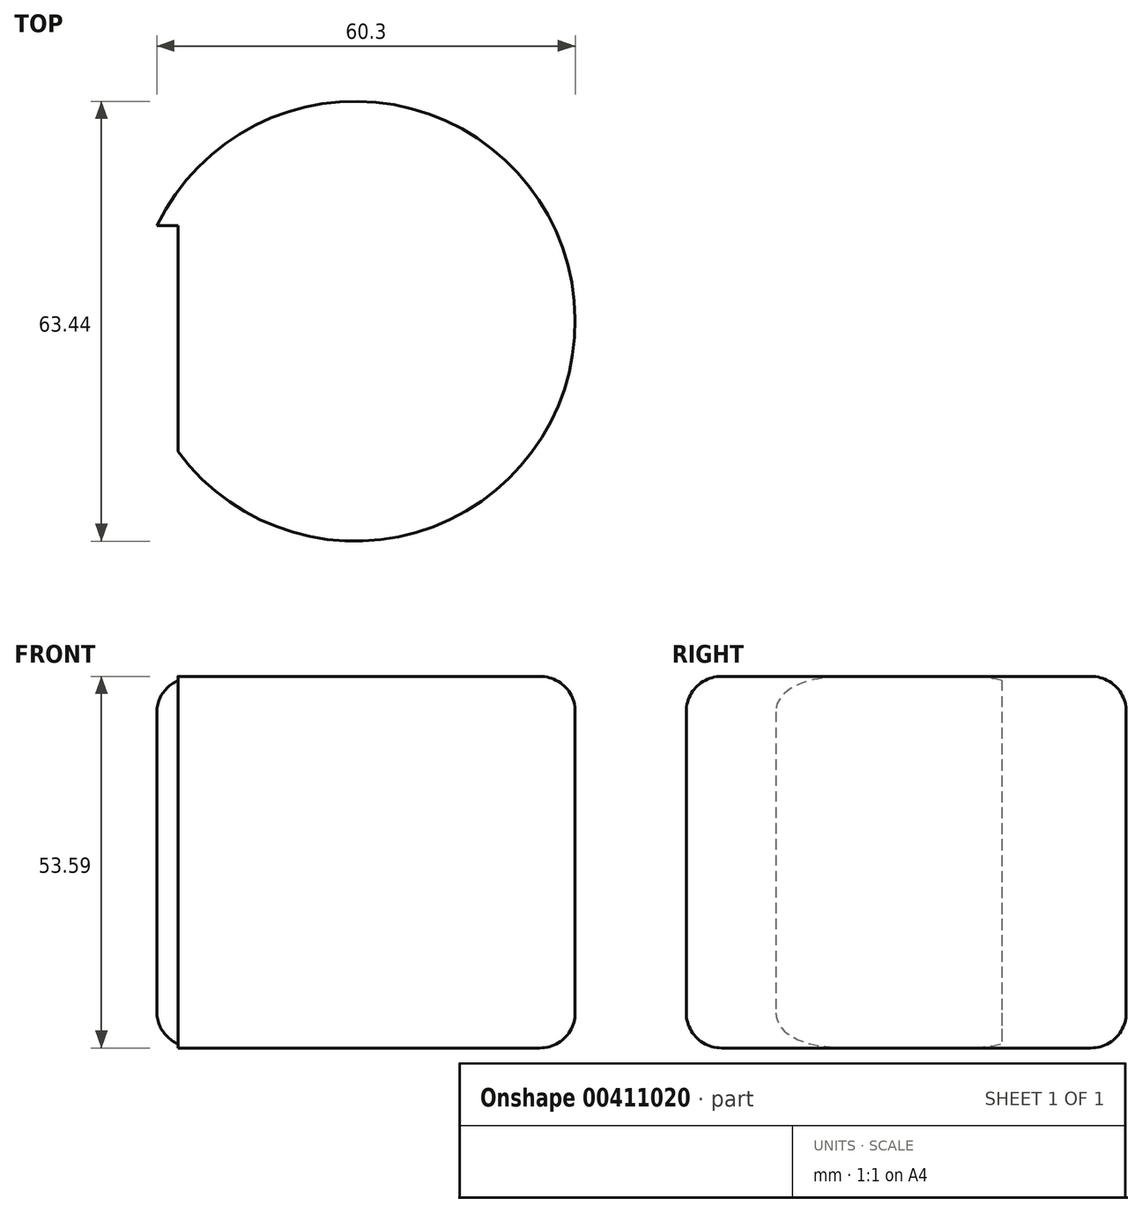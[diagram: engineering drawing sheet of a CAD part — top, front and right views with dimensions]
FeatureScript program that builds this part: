
annotation { "Feature Type Name" : "Feature", "Feature Type Description" : "" }
export const myFeature = defineFeature(function(context is Context, id is Id, definition is map)
    precondition{}
    {
        {
            var Q0;
            Q0=qCreatedBy(makeId("Top.planeOp"),FACE);
            var sketch = newSketch(context, id + "F0", { "sketchPlane" : qUnion([Q0])});
            skCircle(sketch, "E0", {"center": v(0, 0) * mm, "radius": 31.72 * mm});
            skSolve(sketch);
        }
        {
            var Q0;
            Q0 = qSketchRegion(id + "F0", true);
            extrude(context, id + "F1", {"entities" : qUnion([Q0]), "depth" : 53.6 * mm});
        }
        {
            var Q0;
            Q0=makeQuery(id+"F1.opExtrude","CAP_EDGE",EDGE,{"disambiguationData":[OSD([sQuery(id+"F0.wireOp",EDGE,"E0")])],"isStart":false});
            var Q1;
            Q1=makeQuery(id+"F1.opExtrude","CAP_EDGE",EDGE,{"disambiguationData":[OSD([sQuery(id+"F0.wireOp",EDGE,"E0")])],"isStart":true});
            fillet(context, id + "F2", {"entities" : qUnion([Q0, Q1]), "radius" : 5.08 * mm, "tangentPropagation" : true, "allowEdgeOverflow" : false});
        }
        {
            var Q0;
            Q0=qCreatedBy(makeId("Top.planeOp"),FACE);
            var sketch = newSketch(context, id + "F3", { "sketchPlane" : qUnion([Q0])});
            skLineSegment(sketch, "E1.bottom", {"start": v(-66.02, -37.16) * mm, "end": v(-25.54, -37.16) * mm});
            skLineSegment(sketch, "E1.top", {"start": v(-66.02, 13.76) * mm, "end": v(-25.54, 13.76) * mm});
            skLineSegment(sketch, "E1.left", {"start": v(-66.02, -37.16) * mm, "end": v(-66.02, 13.76) * mm});
            skLineSegment(sketch, "E1.right", {"start": v(-25.54, -37.16) * mm, "end": v(-25.54, 13.76) * mm});
            skSolve(sketch);
        }
        {
            var Q0;
            Q0 = qSketchRegion(id + "F3", true);
            extrude(context, id + "F4", {"entities" : qUnion([Q0]), "operationType" : NewBodyOperationType.REMOVE, "depth" : 132.6 * mm});
        }
    });
